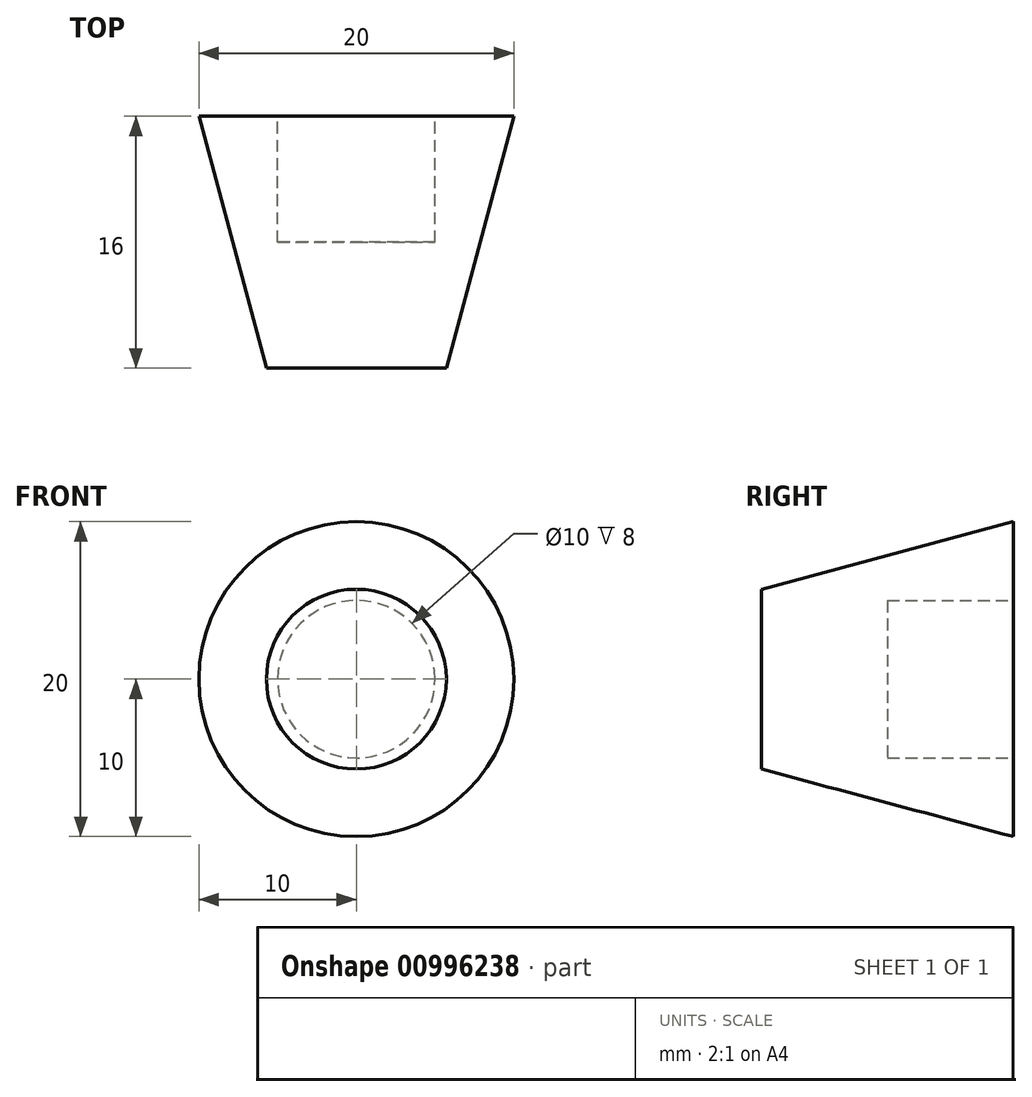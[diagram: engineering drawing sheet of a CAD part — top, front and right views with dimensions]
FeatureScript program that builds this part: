
annotation { "Feature Type Name" : "Feature", "Feature Type Description" : "" }
export const myFeature = defineFeature(function(context is Context, id is Id, definition is map)
    precondition{}
    {
        {
            var Q0;
            Q0=qCreatedBy(makeId("Front.planeOp"),FACE);
            var sketch = newSketch(context, id + "F0", { "sketchPlane" : qUnion([Q0])});
            skCircle(sketch, "E0", {"center": v(0, 0) * mm, "radius": 10 * mm});
            skSolve(sketch);
        }
        {
            var Q0;
            Q0=makeQuery(id+"F0.imprint","IMPRINT",FACE,{"disambiguationData":[TD([[makeQuery(id+"F0.imprint","IMPRINT",EDGE,{"derivedFrom":sQuery(id+"F0.wireOp",EDGE,"E0")}),1.0]])]});
            extrude(context, id + "F1", {"entities" : qUnion([Q0]), "depth" : 16 * mm, "offsetDistance" : 25 * mm, "hasDraft" : true, "draftAngle" : 15 * degree, "draftPullDirection" : true});
        }
        {
            var Q0;
            Q0=makeQuery(id+"F1.opExtrude","CAP_FACE",FACE,{"disambiguationData":[OSD([sQuery(id+"F0.wireOp",EDGE,"E0")])],"isStart":true});
            var sketch = newSketch(context, id + "F2", { "sketchPlane" : qUnion([Q0])});
            skCircle(sketch, "E1", {"center": v(0, 0) * mm, "radius": 5 * mm});
            skSolve(sketch);
        }
        {
            var Q0;
            Q0=makeQuery(id+"F2.imprint","IMPRINT",FACE,{"disambiguationData":[TD([[makeQuery(id+"F2.imprint","IMPRINT",EDGE,{"derivedFrom":sQuery(id+"F2.wireOp",EDGE,"E1")}),1.0]])]});
            extrude(context, id + "F3", {"entities" : qUnion([Q0]), "operationType" : NewBodyOperationType.REMOVE, "oppositeDirection" : true, "depth" : 8 * mm, "offsetDistance" : 25 * mm});
        }
    });
